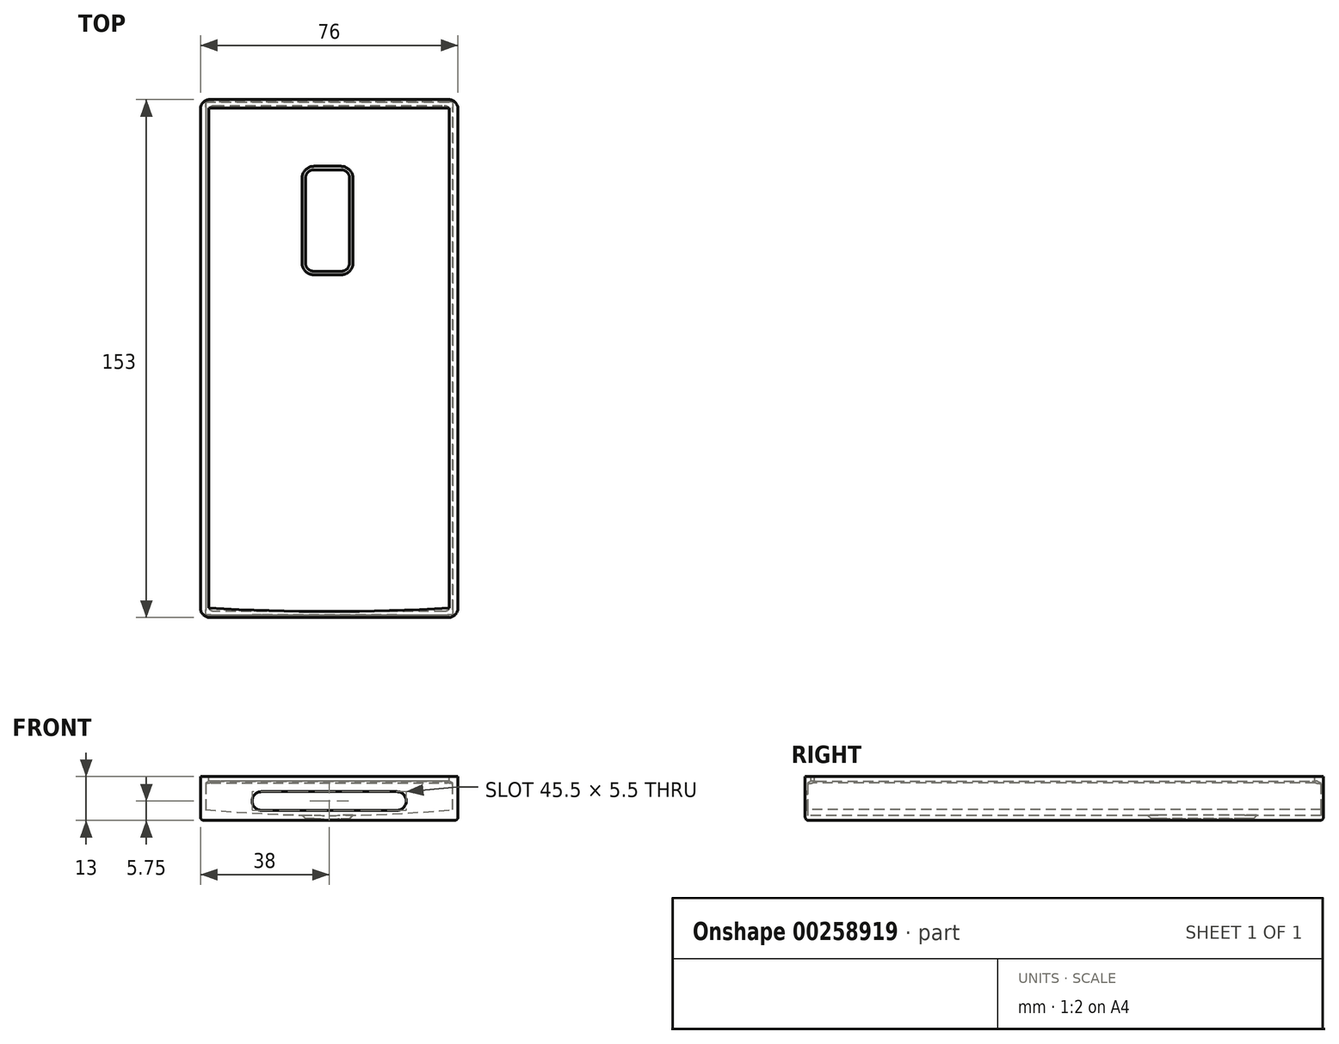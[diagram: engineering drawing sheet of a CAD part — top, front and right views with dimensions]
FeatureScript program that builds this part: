
annotation { "Feature Type Name" : "Feature", "Feature Type Description" : "" }
export const myFeature = defineFeature(function(context is Context, id is Id, definition is map)
    precondition{}
    {
        {
            var Q0;
            Q0=qCreatedBy(makeId("Top.planeOp"),FACE);
            var sketch = newSketch(context, id + "F0", { "sketchPlane" : qUnion([Q0])});
            skLineSegment(sketch, "E0.bottom", {"start": v(-38, 76.5) * mm, "end": v(38, 76.5) * mm});
            skLineSegment(sketch, "E0.top", {"start": v(-38, -76.5) * mm, "end": v(38, -76.5) * mm});
            skLineSegment(sketch, "E0.left", {"start": v(-38, 76.5) * mm, "end": v(-38, -76.5) * mm});
            skLineSegment(sketch, "E0.right", {"start": v(38, 76.5) * mm, "end": v(38, -76.5) * mm});
            skSolve(sketch);
        }
        {
            var Q0;
            Q0=makeQuery(id+"F0.imprint","IMPRINT",FACE,{"disambiguationData":[TD([[makeQuery(id+"F0.imprint","IMPRINT",EDGE,{"derivedFrom":sQuery(id+"F0.wireOp",EDGE,"E0.bottom")}),-1.0]])]});
            extrude(context, id + "F1", {"entities" : qUnion([Q0]), "depth" : 13 * mm});
        }
        {
            var Q0;
            Q0=qCreatedBy(makeId("Front.planeOp"),FACE);
            var sketch = newSketch(context, id + "F2", { "sketchPlane" : qUnion([Q0])});
            skLineSegment(sketch, "E1.0", {"start": v(-36.5, 13) * mm, "end": v(-36.5, 1.5) * mm, "construction": true});
            skLineSegment(sketch, "E1.1", {"start": v(-36.5, 1.5) * mm, "end": v(36.5, 1.5) * mm, "construction": true});
            skLineSegment(sketch, "E1.2", {"start": v(36.5, 13) * mm, "end": v(36.5, 1.5) * mm, "construction": true});
            skPoint(sketch, "E2", {"position": v(0, 1.5) * mm});
            skArc(sketch, "E3", {"start": v(-36.5, 3.25) * mm, "mid": v(0, 1.5) * mm, "end": v(36.5, 3.25) * mm});
            skLineSegment(sketch, "E4.0", {"start": v(-38, 11.65) * mm, "end": v(38, 11.65) * mm, "construction": true});
            skPoint(sketch, "E5", {"position": v(36.5, 11.65) * mm});
            skPoint(sketch, "E6", {"position": v(-36.5, 11.65) * mm});
            skLineSegment(sketch, "E7", {"start": v(-36.5, 11.65) * mm, "end": v(-36.5, 3.25) * mm});
            skLineSegment(sketch, "E8", {"start": v(-36.5, 11.65) * mm, "end": v(36.5, 11.65) * mm});
            skLineSegment(sketch, "E9", {"start": v(36.5, 3.25) * mm, "end": v(36.5, 11.65) * mm});
            skSolve(sketch);
        }
        {
            var Q0;
            Q0 = qSketchRegion(id + "F2", true);
            extrude(context, id + "F3", {"entities" : qUnion([Q0]), "operationType" : NewBodyOperationType.REMOVE, "oppositeDirection" : true, "depth" : (151.5 / 2) * mm, "hasSecondDirection" : true, "secondDirectionOppositeDirection" : false, "secondDirectionDepth" : (151.5 / 2) * mm});
        }
        {
            var Q0;
            Q0=makeQuery(id+"F1.opExtrude","CAP_FACE",FACE,{"disambiguationData":[OSD([sQuery(id+"F0.wireOp",EDGE,"E0.bottom"),sQuery(id+"F0.wireOp",EDGE,"E0.top"),sQuery(id+"F0.wireOp",EDGE,"E0.left"),sQuery(id+"F0.wireOp",EDGE,"E0.right")])],"isStart":false});
            var sketch = newSketch(context, id + "F4", { "sketchPlane" : qUnion([Q0])});
            skLineSegment(sketch, "E10.0", {"start": v(-35.5, 74) * mm, "end": v(-35.5, -73.75) * mm});
            skLineSegment(sketch, "E10.1", {"start": v(-35.5, 74) * mm, "end": v(35.5, 74) * mm});
            skLineSegment(sketch, "E10.2", {"start": v(35.5, 74) * mm, "end": v(35.5, -73.75) * mm});
            skLineSegment(sketch, "E11.0", {"start": v(-38, -74.75) * mm, "end": v(38, -74.75) * mm, "construction": true});
            skPoint(sketch, "E12", {"position": v(0, -74.75) * mm});
            skArc(sketch, "E13", {"start": v(-35.5, -73.75) * mm, "mid": v(0, -74.75) * mm, "end": v(35.5, -73.75) * mm});
            skSolve(sketch);
        }
        {
            var Q0;
            Q0 = qSketchRegion(id + "F4", true);
            extrude(context, id + "F5", {"entities" : qUnion([Q0]), "operationType" : NewBodyOperationType.REMOVE, "oppositeDirection" : true, "depth" : 1.5 * mm});
        }
        {
            var Q0;
            Q0=makeQuery(id+"F3.boolean.opBoolean","COPY",EDGE,{"derivedFrom":makeQuery(id+"F3.opExtrude","SWEPT_EDGE",EDGE,{"disambiguationData":[OSD([sQuery(id+"F2.wireOp",EDGE,"E7"),sQuery(id+"F2.wireOp",EDGE,"E8")])]})});
            var Q1;
            Q1=makeQuery(id+"F3.boolean.opBoolean","COPY",EDGE,{"derivedFrom":makeQuery(id+"F3.opExtrude","SWEPT_EDGE",EDGE,{"disambiguationData":[OSD([sQuery(id+"F2.wireOp",EDGE,"E8"),sQuery(id+"F2.wireOp",EDGE,"E9")])]})});
            chamfer(context, id + "F6", {"entities" : qUnion([Q0, Q1]), "chamferType" : ChamferType.TWO_OFFSETS, "width1" : .6 * mm, "oppositeDirection" : false, "width2" : 1 * mm, "tangentPropagation" : true});
        }
        {
            var Q0;
            Q0=makeQuery(id+"F3.boolean.opBoolean","COPY",EDGE,{"derivedFrom":makeQuery(id+"F3.opExtrude","CAP_EDGE",EDGE,{"disambiguationData":[OSD([sQuery(id+"F2.wireOp",EDGE,"E8")])],"isStart":false})});
            chamfer(context, id + "F7", {"entities" : qUnion([Q0]), "chamferType" : ChamferType.TWO_OFFSETS, "width1" : 1 * mm, "oppositeDirection" : false, "width2" : .6 * mm, "tangentPropagation" : true});
        }
        {
            var Q0;
            Q0=makeQuery(id+"F3.boolean.opBoolean","COPY",EDGE,{"derivedFrom":makeQuery(id+"F3.opExtrude","CAP_EDGE",EDGE,{"disambiguationData":[OSD([sQuery(id+"F2.wireOp",EDGE,"E8")])],"isStart":true})});
            chamfer(context, id + "F8", {"entities" : qUnion([Q0]), "chamferType" : ChamferType.TWO_OFFSETS, "width1" : .6 * mm, "oppositeDirection" : false, "width2" : 1 * mm, "tangentPropagation" : true});
        }
        {
            var Q0;
            {var subQ0=sQuery(id+"F2.wireOp",EDGE,"E8");Q0=makeQuery(id+"F8.opChamfer","BLEND_EDGE",EDGE,{"blendedFrom":[makeQuery(id+"F3.boolean.opBoolean","COPY",EDGE,{"derivedFrom":makeQuery(id+"F3.opExtrude","CAP_EDGE",EDGE,{"disambiguationData":[OSD([subQ0])],"isStart":true})}),makeQuery(id+"F6.opChamfer","BLEND_FACE",FACE,{"disambiguationData":[OSD([subQ0,sQuery(id+"F2.wireOp",EDGE,"E9")])]})],"blendedInto":[makeQuery(id+"F6.opChamfer","BLEND_FACE",FACE,{"disambiguationData":[OSD([subQ0,sQuery(id+"F2.wireOp",EDGE,"E9")])]})]});}
            var Q1;
            {var subQ0=sQuery(id+"F2.wireOp",EDGE,"E8");Q1=makeQuery(id+"F8.opChamfer","BLEND_EDGE",EDGE,{"blendedFrom":[makeQuery(id+"F3.boolean.opBoolean","COPY",EDGE,{"derivedFrom":makeQuery(id+"F3.opExtrude","CAP_EDGE",EDGE,{"disambiguationData":[OSD([subQ0])],"isStart":true})}),makeQuery(id+"F6.opChamfer","BLEND_FACE",FACE,{"disambiguationData":[OSD([sQuery(id+"F2.wireOp",EDGE,"E7"),subQ0])]})],"blendedInto":[makeQuery(id+"F6.opChamfer","BLEND_FACE",FACE,{"disambiguationData":[OSD([sQuery(id+"F2.wireOp",EDGE,"E7"),subQ0])]})]});}
            var Q2;
            {var subQ0=sQuery(id+"F2.wireOp",EDGE,"E8");Q2=makeQuery(id+"F7.opChamfer","BLEND_EDGE",EDGE,{"blendedFrom":[makeQuery(id+"F3.boolean.opBoolean","COPY",EDGE,{"derivedFrom":makeQuery(id+"F3.opExtrude","CAP_EDGE",EDGE,{"disambiguationData":[OSD([subQ0])],"isStart":false})}),makeQuery(id+"F6.opChamfer","BLEND_FACE",FACE,{"disambiguationData":[OSD([sQuery(id+"F2.wireOp",EDGE,"E7"),subQ0])]})],"blendedInto":[makeQuery(id+"F6.opChamfer","BLEND_FACE",FACE,{"disambiguationData":[OSD([sQuery(id+"F2.wireOp",EDGE,"E7"),subQ0])]})]});}
            var Q3;
            {var subQ0=sQuery(id+"F2.wireOp",EDGE,"E8");Q3=makeQuery(id+"F7.opChamfer","BLEND_EDGE",EDGE,{"blendedFrom":[makeQuery(id+"F3.boolean.opBoolean","COPY",EDGE,{"derivedFrom":makeQuery(id+"F3.opExtrude","CAP_EDGE",EDGE,{"disambiguationData":[OSD([subQ0])],"isStart":false})}),makeQuery(id+"F6.opChamfer","BLEND_FACE",FACE,{"disambiguationData":[OSD([subQ0,sQuery(id+"F2.wireOp",EDGE,"E9")])]})],"blendedInto":[makeQuery(id+"F6.opChamfer","BLEND_FACE",FACE,{"disambiguationData":[OSD([subQ0,sQuery(id+"F2.wireOp",EDGE,"E9")])]})]});}
            fillet(context, id + "F9", {"entities" : qUnion([Q0, Q1, Q2, Q3]), "radius" : 3 * mm, "tangentPropagation" : true, "allowEdgeOverflow" : false});
        }
        {
            var Q0;
            Q0=qCreatedBy(makeId("Top.planeOp"),FACE);
            var sketch = newSketch(context, id + "F10", { "sketchPlane" : qUnion([Q0])});
            skLineSegment(sketch, "E14.bottom", {"start": v(3.5, 25.75) * mm, "end": v(-4.5, 25.75) * mm});
            skLineSegment(sketch, "E14.top", {"start": v(3.5, 55.75) * mm, "end": v(-4.5, 55.75) * mm});
            skLineSegment(sketch, "E14.left", {"start": v(6, 53.25) * mm, "end": v(6, 28.25) * mm});
            skLineSegment(sketch, "E14.right", {"start": v(-7, 53.25) * mm, "end": v(-7, 28.25) * mm});
            skPoint(sketch, "E15.visualSharp", {"position": v(6, 55.75) * mm});
            skArc(sketch, "E15.filletArc", {"start": v(6, 53.25) * mm, "mid": v(5.27, 55.02) * mm, "end": v(3.5, 55.75) * mm});
            skPoint(sketch, "E16.visualSharp", {"position": v(-7, 55.75) * mm});
            skArc(sketch, "E16.filletArc", {"start": v(-4.5, 55.75) * mm, "mid": v(-6.27, 55.02) * mm, "end": v(-7, 53.25) * mm});
            skPoint(sketch, "E17.visualSharp", {"position": v(-7, 25.75) * mm});
            skArc(sketch, "E17.filletArc", {"start": v(-7, 28.25) * mm, "mid": v(-6.27, 26.48) * mm, "end": v(-4.5, 25.75) * mm});
            skPoint(sketch, "E18.visualSharp", {"position": v(6, 25.75) * mm});
            skArc(sketch, "E18.filletArc", {"start": v(3.5, 25.75) * mm, "mid": v(5.27, 26.48) * mm, "end": v(6, 28.25) * mm});
            skSolve(sketch);
        }
        {
            var Q0;
            Q0 = qSketchRegion(id + "F10", true);
            extrude(context, id + "F11", {"entities" : qUnion([Q0]), "operationType" : NewBodyOperationType.REMOVE, "depth" : 25 * mm});
        }
        {
            var Q0;
            Q0=makeQuery(id+"F11.boolean.opBoolean","INTERSECT",EDGE,{"derivedFrom":[makeQuery(id+"F3.boolean.opBoolean","COPY",FACE,{"derivedFrom":makeQuery(id+"F3.opExtrude","SWEPT_FACE",FACE,{"disambiguationData":[OSD([sQuery(id+"F2.wireOp",EDGE,"E3")])]})}),makeQuery(id+"F11.opExtrude","SWEPT_FACE",FACE,{"disambiguationData":[OSD([sQuery(id+"F10.wireOp",EDGE,"E14.right")])]})]});
            chamfer(context, id + "F12", {"entities" : qUnion([Q0]), "chamferType" : ChamferType.OFFSET_ANGLE, "width" : 1 * mm, "oppositeDirection" : false, "angle" : 45 * degree, "tangentPropagation" : true});
        }
        {
            var Q0;
            Q0=makeQuery(id+"F1.opExtrude","SWEPT_EDGE",EDGE,{"disambiguationData":[OSD([sQuery(id+"F0.wireOp",EDGE,"E0.bottom"),sQuery(id+"F0.wireOp",EDGE,"E0.right")])]});
            var Q1;
            Q1=makeQuery(id+"F1.opExtrude","SWEPT_EDGE",EDGE,{"disambiguationData":[OSD([sQuery(id+"F0.wireOp",EDGE,"E0.bottom"),sQuery(id+"F0.wireOp",EDGE,"E0.left")])]});
            var Q2;
            Q2=makeQuery(id+"F1.opExtrude","SWEPT_EDGE",EDGE,{"disambiguationData":[OSD([sQuery(id+"F0.wireOp",EDGE,"E0.top"),sQuery(id+"F0.wireOp",EDGE,"E0.right")])]});
            var Q3;
            Q3=makeQuery(id+"F1.opExtrude","SWEPT_EDGE",EDGE,{"disambiguationData":[OSD([sQuery(id+"F0.wireOp",EDGE,"E0.top"),sQuery(id+"F0.wireOp",EDGE,"E0.left")])]});
            fillet(context, id + "F13", {"entities" : qUnion([Q0, Q1, Q2, Q3]), "radius" : 2.75 * mm, "tangentPropagation" : true, "allowEdgeOverflow" : false});
        }
        {
            var Q0;
            Q0=makeQuery(id+"F1.opExtrude","CAP_EDGE",EDGE,{"disambiguationData":[OSD([sQuery(id+"F0.wireOp",EDGE,"E0.top")])],"isStart":true});
            var Q1;
            Q1=makeQuery(id+"F1.opExtrude","CAP_EDGE",EDGE,{"disambiguationData":[OSD([sQuery(id+"F0.wireOp",EDGE,"E0.left")])],"isStart":true});
            var Q2;
            {var subQ0=sQuery(id+"F0.wireOp",EDGE,"E0.left");var subQ1=sQuery(id+"F0.wireOp",EDGE,"E0.top");Q2=makeQuery(id+"F13.opFillet","BLEND_EDGE",EDGE,{"blendedFrom":[makeQuery(id+"F1.opExtrude","SWEPT_EDGE",EDGE,{"disambiguationData":[OSD([subQ1,subQ0])]}),makeQuery(id+"F1.opExtrude","CAP_FACE",FACE,{"disambiguationData":[OSD([sQuery(id+"F0.wireOp",EDGE,"E0.bottom"),subQ1,subQ0,sQuery(id+"F0.wireOp",EDGE,"E0.right")])],"isStart":true})],"blendedInto":[makeQuery(id+"F1.opExtrude","CAP_FACE",FACE,{"disambiguationData":[OSD([sQuery(id+"F0.wireOp",EDGE,"E0.bottom"),subQ1,subQ0,sQuery(id+"F0.wireOp",EDGE,"E0.right")])],"isStart":true})]});}
            var Q3;
            {var subQ0=sQuery(id+"F0.wireOp",EDGE,"E0.right");var subQ1=sQuery(id+"F0.wireOp",EDGE,"E0.top");Q3=makeQuery(id+"F13.opFillet","BLEND_EDGE",EDGE,{"blendedFrom":[makeQuery(id+"F1.opExtrude","SWEPT_EDGE",EDGE,{"disambiguationData":[OSD([subQ1,subQ0])]}),makeQuery(id+"F1.opExtrude","CAP_FACE",FACE,{"disambiguationData":[OSD([sQuery(id+"F0.wireOp",EDGE,"E0.bottom"),subQ1,sQuery(id+"F0.wireOp",EDGE,"E0.left"),subQ0])],"isStart":true})],"blendedInto":[makeQuery(id+"F1.opExtrude","CAP_FACE",FACE,{"disambiguationData":[OSD([sQuery(id+"F0.wireOp",EDGE,"E0.bottom"),subQ1,sQuery(id+"F0.wireOp",EDGE,"E0.left"),subQ0])],"isStart":true})]});}
            var Q4;
            Q4=makeQuery(id+"F1.opExtrude","CAP_EDGE",EDGE,{"disambiguationData":[OSD([sQuery(id+"F0.wireOp",EDGE,"E0.right")])],"isStart":true});
            var Q5;
            {var subQ0=sQuery(id+"F0.wireOp",EDGE,"E0.right");var subQ1=sQuery(id+"F0.wireOp",EDGE,"E0.bottom");Q5=makeQuery(id+"F13.opFillet","BLEND_EDGE",EDGE,{"blendedFrom":[makeQuery(id+"F1.opExtrude","SWEPT_EDGE",EDGE,{"disambiguationData":[OSD([subQ1,subQ0])]}),makeQuery(id+"F1.opExtrude","CAP_FACE",FACE,{"disambiguationData":[OSD([subQ1,sQuery(id+"F0.wireOp",EDGE,"E0.top"),sQuery(id+"F0.wireOp",EDGE,"E0.left"),subQ0])],"isStart":true})],"blendedInto":[makeQuery(id+"F1.opExtrude","CAP_FACE",FACE,{"disambiguationData":[OSD([subQ1,sQuery(id+"F0.wireOp",EDGE,"E0.top"),sQuery(id+"F0.wireOp",EDGE,"E0.left"),subQ0])],"isStart":true})]});}
            var Q6;
            Q6=makeQuery(id+"F1.opExtrude","CAP_EDGE",EDGE,{"disambiguationData":[OSD([sQuery(id+"F0.wireOp",EDGE,"E0.bottom")])],"isStart":true});
            var Q7;
            {var subQ0=sQuery(id+"F0.wireOp",EDGE,"E0.left");var subQ1=sQuery(id+"F0.wireOp",EDGE,"E0.bottom");Q7=makeQuery(id+"F13.opFillet","BLEND_EDGE",EDGE,{"blendedFrom":[makeQuery(id+"F1.opExtrude","SWEPT_EDGE",EDGE,{"disambiguationData":[OSD([subQ1,subQ0])]}),makeQuery(id+"F1.opExtrude","CAP_FACE",FACE,{"disambiguationData":[OSD([subQ1,sQuery(id+"F0.wireOp",EDGE,"E0.top"),subQ0,sQuery(id+"F0.wireOp",EDGE,"E0.right")])],"isStart":true})],"blendedInto":[makeQuery(id+"F1.opExtrude","CAP_FACE",FACE,{"disambiguationData":[OSD([subQ1,sQuery(id+"F0.wireOp",EDGE,"E0.top"),subQ0,sQuery(id+"F0.wireOp",EDGE,"E0.right")])],"isStart":true})]});}
            fillet(context, id + "F14", {"entities" : qUnion([Q0, Q1, Q2, Q3, Q4, Q5, Q6, Q7]), "radius" : 1 * mm, "tangentPropagation" : true, "allowEdgeOverflow" : false});
        }
        {
            var Q0;
            Q0=makeQuery(id+"F1.opExtrude","SWEPT_FACE",FACE,{"disambiguationData":[OSD([sQuery(id+"F0.wireOp",EDGE,"E0.top")])]});
            var sketch = newSketch(context, id + "F15", { "sketchPlane" : qUnion([Q0])});
            skLineSegment(sketch, "E19", {"start": v(-20, 5.75) * mm, "end": v(20, 5.75) * mm, "construction": true});
            skPoint(sketch, "E20", {"position": v(0, 5.75) * mm});
            skPoint(sketch, "E20.positionSnap0", {"position": v(0, 13) * mm});
            skArc(sketch, "E21.0.startCap", {"start": v(-20, 3) * mm, "mid": v(-22.75, 5.75) * mm, "end": v(-20, 8.5) * mm});
            skArc(sketch, "E21.0.endCap", {"start": v(20, 8.5) * mm, "mid": v(22.75, 5.75) * mm, "end": v(20, 3) * mm});
            skLineSegment(sketch, "E21.0.left", {"start": v(-20, 8.5) * mm, "end": v(20, 8.5) * mm});
            skLineSegment(sketch, "E21.0.right", {"start": v(-20, 3) * mm, "end": v(20, 3) * mm});
            skSolve(sketch);
        }
        {
            var Q0;
            Q0 = qSketchRegion(id + "F15", true);
            extrude(context, id + "F16", {"entities" : qUnion([Q0]), "operationType" : NewBodyOperationType.REMOVE, "endBound" : BoundingType.UP_TO_NEXT, "oppositeDirection" : true, "depth" : 25 * mm});
        }
    });
